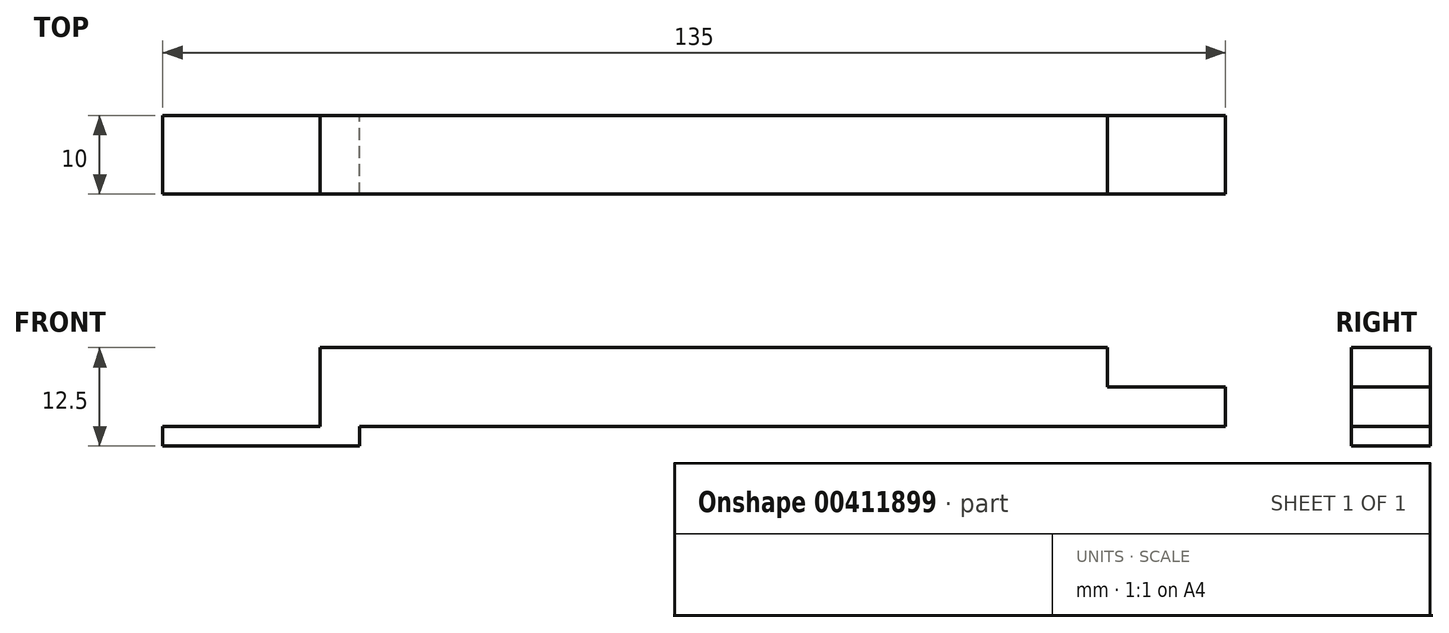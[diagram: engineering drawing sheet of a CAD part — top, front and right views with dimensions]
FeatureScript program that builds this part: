
annotation { "Feature Type Name" : "Feature", "Feature Type Description" : "" }
export const myFeature = defineFeature(function(context is Context, id is Id, definition is map)
    precondition{}
    {
        {
            var Q0;
            Q0=qCreatedBy(makeId("Front.planeOp"),FACE);
            var sketch = newSketch(context, id + "F0", { "sketchPlane" : qUnion([Q0])});
            skLineSegment(sketch, "E0.bottom", {"start": v(-57.5, 0) * mm, "end": v(57.5, 0) * mm});
            skLineSegment(sketch, "E0.top", {"start": v(-57.5, -10) * mm, "end": v(57.5, -10) * mm});
            skLineSegment(sketch, "E0.left", {"start": v(-57.5, 0) * mm, "end": v(-57.5, -10) * mm});
            skLineSegment(sketch, "E0.right", {"start": v(57.5, 0) * mm, "end": v(57.5, -10) * mm});
            skSolve(sketch);
        }
        {
            var Q0;
            Q0 = qSketchRegion(id + "F0", true);
            extrude(context, id + "F1", {"entities" : qUnion([Q0]), "depth" : 10 * mm});
        }
        {
            var Q0;
            Q0=makeQuery(id+"F1.opExtrude","SWEPT_FACE",FACE,{"disambiguationData":[OSD([sQuery(id+"F0.wireOp",EDGE,"E0.bottom")])]});
            var sketch = newSketch(context, id + "F2", { "sketchPlane" : qUnion([Q0])});
            skLineSegment(sketch, "E1.bottom", {"start": v(42.5, 0) * mm, "end": v(57.5, 0) * mm});
            skLineSegment(sketch, "E1.top", {"start": v(42.5, -10) * mm, "end": v(57.5, -10) * mm});
            skLineSegment(sketch, "E1.left", {"start": v(42.5, 0) * mm, "end": v(42.5, -10) * mm});
            skLineSegment(sketch, "E1.right", {"start": v(57.5, 0) * mm, "end": v(57.5, -10) * mm});
            skSolve(sketch);
        }
        {
            var Q0;
            Q0=makeQuery(id+"F2.imprint","IMPRINT",FACE,{"disambiguationData":[TD([[makeQuery(id+"F2.imprint","IMPRINT",EDGE,{"derivedFrom":sQuery(id+"F2.wireOp",EDGE,"E1.bottom")}),-1.0]])]});
            extrude(context, id + "F3", {"entities" : qUnion([Q0]), "operationType" : NewBodyOperationType.REMOVE, "oppositeDirection" : true, "depth" : 5 * mm});
        }
        {
            var Q0;
            Q0=makeQuery(id+"F1.opExtrude","SWEPT_FACE",FACE,{"disambiguationData":[OSD([sQuery(id+"F0.wireOp",EDGE,"E0.top")])]});
            var sketch = newSketch(context, id + "F4", { "sketchPlane" : qUnion([Q0])});
            skLineSegment(sketch, "E2.bottom", {"start": v(-52.5, 10) * mm, "end": v(-77.5, 10) * mm});
            skLineSegment(sketch, "E2.top", {"start": v(-52.5, 0) * mm, "end": v(-77.5, 0) * mm});
            skLineSegment(sketch, "E2.left", {"start": v(-52.5, 10) * mm, "end": v(-52.5, 0) * mm});
            skLineSegment(sketch, "E2.right", {"start": v(-77.5, 10) * mm, "end": v(-77.5, 0) * mm});
            skSolve(sketch);
        }
        {
            var Q0;
            Q0 = qSketchRegion(id + "F4", true);
            extrude(context, id + "F5", {"entities" : qUnion([Q0]), "operationType" : NewBodyOperationType.ADD, "depth" : 2.5 * mm});
        }
    });
